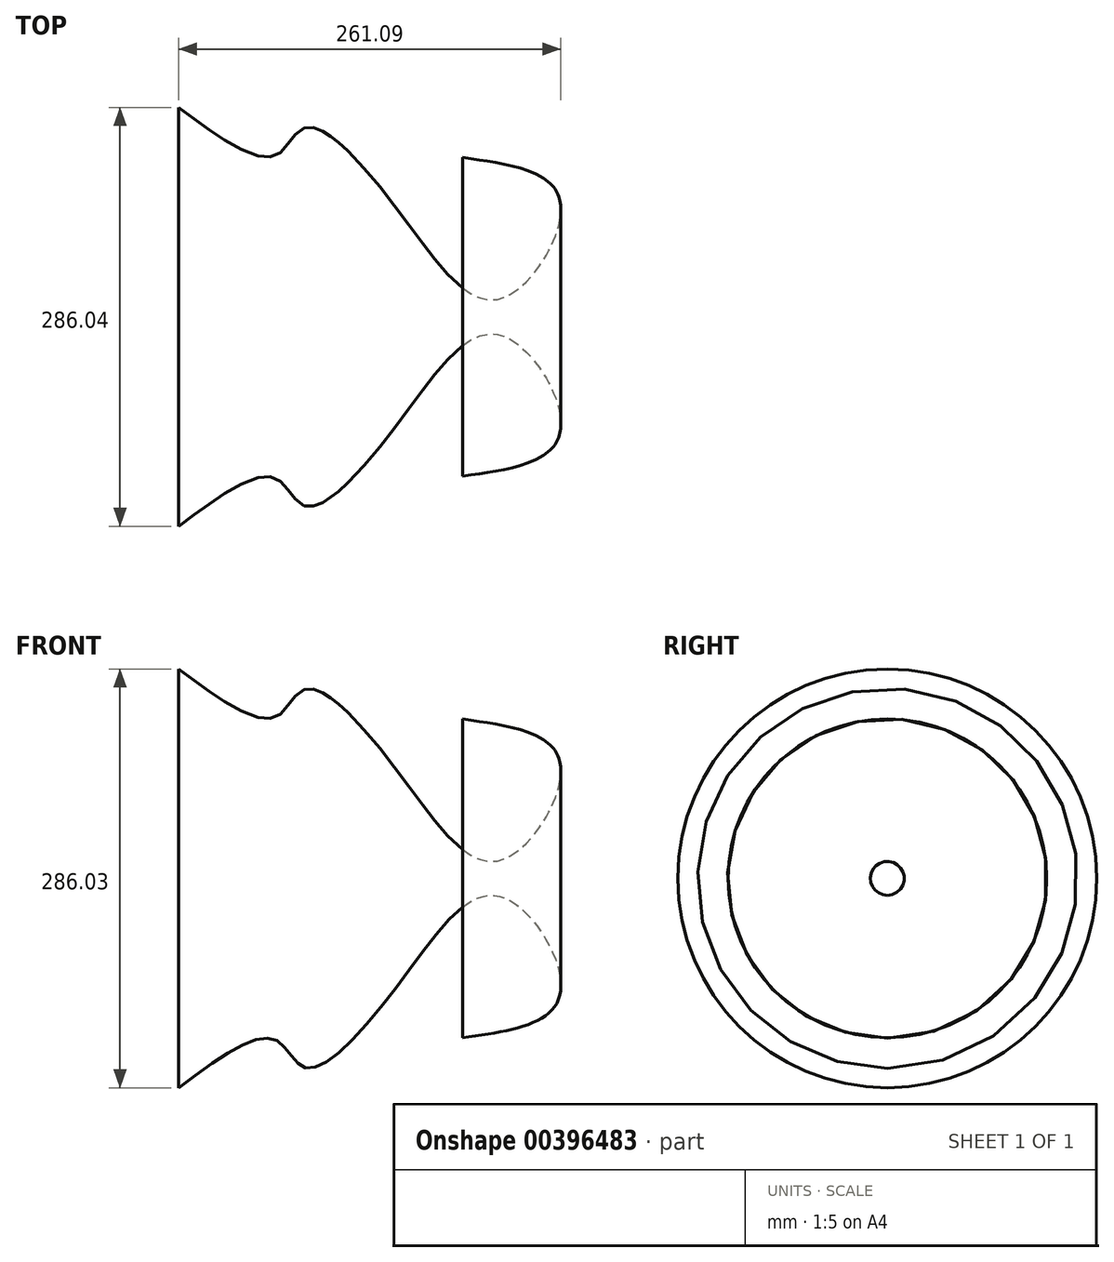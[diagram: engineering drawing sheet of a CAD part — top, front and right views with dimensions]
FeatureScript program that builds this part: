
annotation { "Feature Type Name" : "Feature", "Feature Type Description" : "" }
export const myFeature = defineFeature(function(context is Context, id is Id, definition is map)
    precondition{}
    {
        {
            var Q0;
            Q0=qCreatedBy(makeId("Front.planeOp"),FACE);
            var sketch = newSketch(context, id + "F0", { "sketchPlane" : qUnion([Q0])});
            skFitSpline(sketch, "E0", {"points": [v(-149.38, -69.5) * mm, v(-83.43, -36.61) * mm, v(-62.98, -55.77) * mm, v(0, 0) * mm, v(69.58, 61.3) * mm, v(111.13, -5.84) * mm, v(44.52, -35.3) * mm], "startDerivative": vector(455.92, 339.4) * mm, "endDerivative": vector(-547.18, -74.82) * mm});
            skLineSegment(sketch, "E1", {"start": v(-85.74, 73.52) * mm, "end": v(148.72, 73.52) * mm});
            skSolve(sketch);
        }
        {
            var Q0;
            Q0=sQuery(id+"F0.wireOp",EDGE,"E0");
            var Q1;
            Q1=sQuery(id+"F0.wireOp",EDGE,"E1");
            revolve(context, id + "F1", {"bodyType" : ToolBodyType.SURFACE, "surfaceEntities" : qUnion([Q0]), "axis" : qUnion([Q1]), "revolveType" : RevolveType.FULL});
        }
    });
